# Revit family: Furniture_Tables_Svedholm_Arc-table
name_source: partatom
category: Furniture
revit_build: Autodesk Revit 2018 (Build: 20190510_1515(x64)
units: mm (PartAtom-declared; Revit-internal decimal feet)

## family parameters
Always vertical = Yes
Cut with Voids When Loaded = No
OmniClass Number = 23.21.23.00
OmniClass Title = Residential Furniture and Equipment
Room Calculation Point = No
Shared = No
Work Plane-Based = Yes

## types (2) — shared parameters
BIMobject category = Tables
Default Elevation = 1219 mm
Description = A side table of wire. Table top of tempered glass with ceramic paint alternatively marble. Table base of powder coated wire.
Detail material = Svedholm - Metal - RAL 9005 Jet black
Edition number = 1
IFC Classification = Furniture
Manufacturer = Svedholm
Manufacturer name = Svedholm
Model = Arc table
OmniClass Code = 23-21 23 00
OmniClass Description = Residential Furniture and Equipment
Product Guid = f3652654-9aa5-435f-8834-e495e352db0b
Product SKU = Arc
Product data url = https://bimobject.com
Product family = Arc
Product group = Tables
Product name = Arc table
Product url = https://www.svedholm.se
QR code = https://bimobject.com
Secondary material = <By Category>
UNSPSC Code = 56
URL = https://www.svedholm.se
Uniclass 1.4 Code = L8221
Uniclass 1.4 Description = Tables

## per-type parameters (varying)
| type | Glass | Marble |
| ART - (205.600.001) Tabletop material - (Glass) | Yes | No |
| ART - (205.600.002) Tabletop material - (Marble) | No | Yes |

## geometry (parser evidence)
native form markers: Sweep x6
no freeform markers — native parametric forms only
